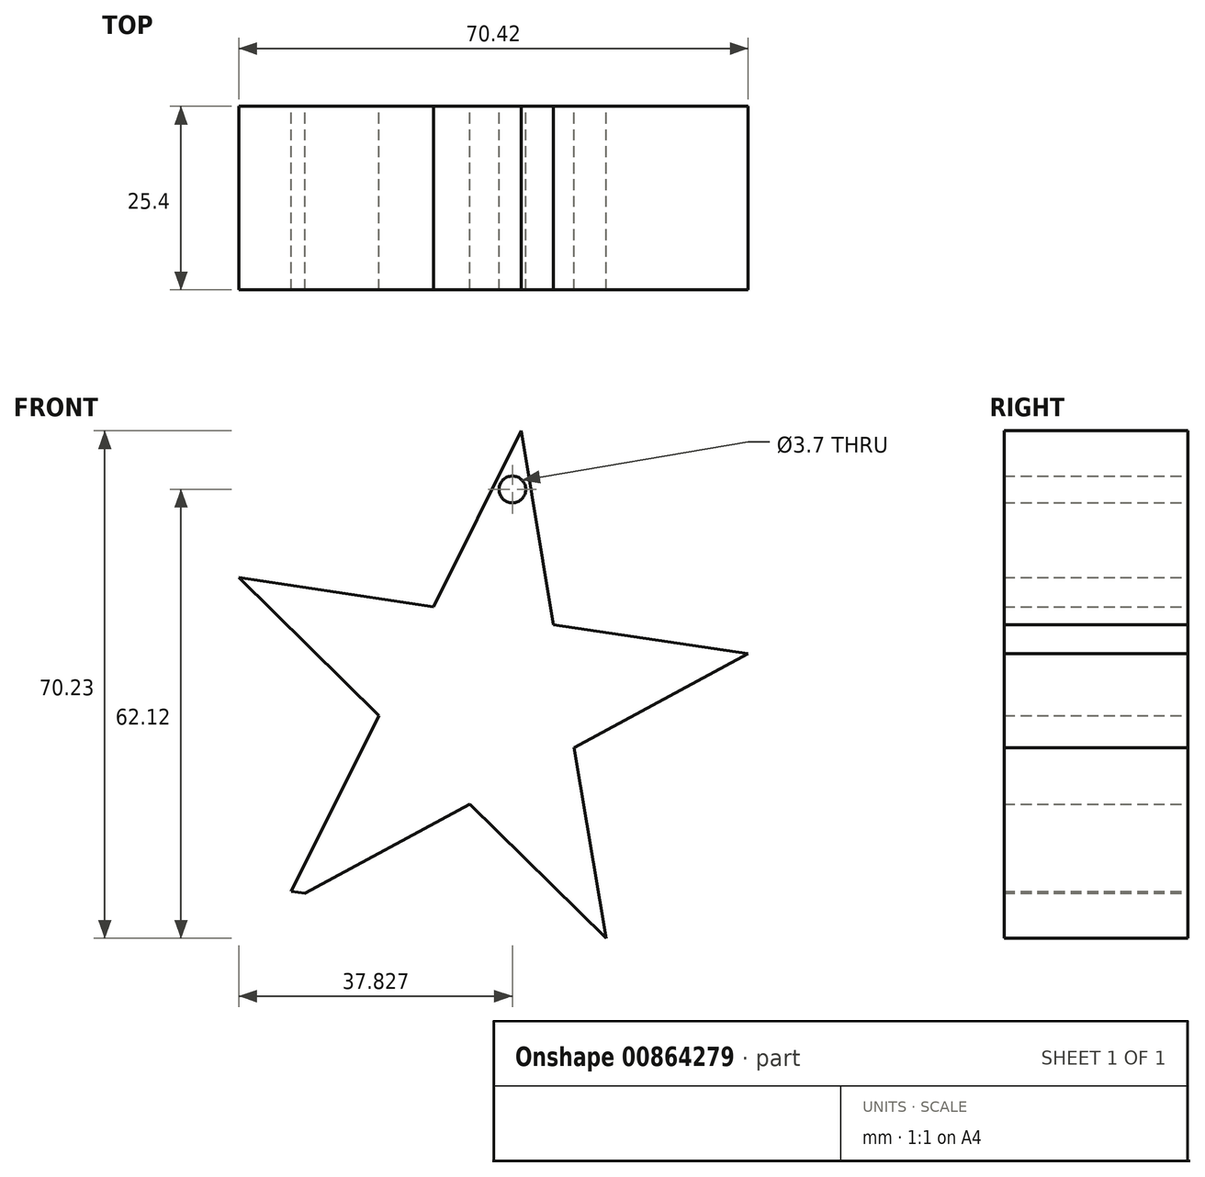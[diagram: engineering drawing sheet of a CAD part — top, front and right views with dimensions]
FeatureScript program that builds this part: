
annotation { "Feature Type Name" : "Feature", "Feature Type Description" : "" }
export const myFeature = defineFeature(function(context is Context, id is Id, definition is map)
    precondition{}
    {
        {
            var Q0;
            Q0=qCreatedBy(makeId("Front.planeOp"),FACE);
            var sketch = newSketch(context, id + "F0", { "sketchPlane" : qUnion([Q0])});
            skCircle(sketch, "E0.cCircle", {"center": v(0, 0) * mm, "radius": 37.44 * mm, "construction": true});
            skLineSegment(sketch, "E0.4", {"start": v(-24.34, -26.98) * mm, "end": v(-26.24, -26.7) * mm});
            skLineSegment(sketch, "E1", {"start": v(-26.24, -26.7) * mm, "end": v(-14.1, -2.36) * mm});
            skLineSegment(sketch, "E2", {"start": v(5.53, 37.02) * mm, "end": v(10.02, 10.2) * mm});
            skLineSegment(sketch, "E3", {"start": v(17.29, -33.2) * mm, "end": v(-1.58, -14.66) * mm});
            skLineSegment(sketch, "E4", {"start": v(-33.5, 16.7) * mm, "end": v(-6.6, 12.68) * mm});
            skLineSegment(sketch, "E5", {"start": v(36.92, 6.18) * mm, "end": v(12.87, -6.84) * mm});
            skLineSegment(sketch, "E6.trimOffspring", {"start": v(12.87, -6.84) * mm, "end": v(17.29, -33.2) * mm});
            skLineSegment(sketch, "E7.trimOffspring", {"start": v(10.02, 10.2) * mm, "end": v(36.92, 6.18) * mm});
            skLineSegment(sketch, "E8.trimOffspring", {"start": v(-6.6, 12.68) * mm, "end": v(5.53, 37.02) * mm});
            skLineSegment(sketch, "E9.trimOffspring", {"start": v(-14.1, -2.36) * mm, "end": v(-33.5, 16.7) * mm});
            skLineSegment(sketch, "E10.trimOffspring", {"start": v(-1.58, -14.66) * mm, "end": v(-25.36, -27.54) * mm});
            skCircle(sketch, "E11", {"center": v(4.33, 28.91) * mm, "radius": 1.85 * mm});
            skSolve(sketch);
        }
        {
            var Q0;
            {var subQ0=sQuery(id+"F0.wireOp",EDGE,"E0.4");Q0=makeQuery(id+"F0.imprint","IMPRINT",FACE,{"disambiguationData":[TD([[makeQuery(id+"F0.imprint","IMPRINT",EDGE,{"derivedFrom":subQ0}),-1.0]])]});}
            extrude(context, id + "F1", {"entities" : qUnion([Q0]), "depth" : 25.4 * mm, "offsetDistance" : 25.4 * mm});
        }
    });
